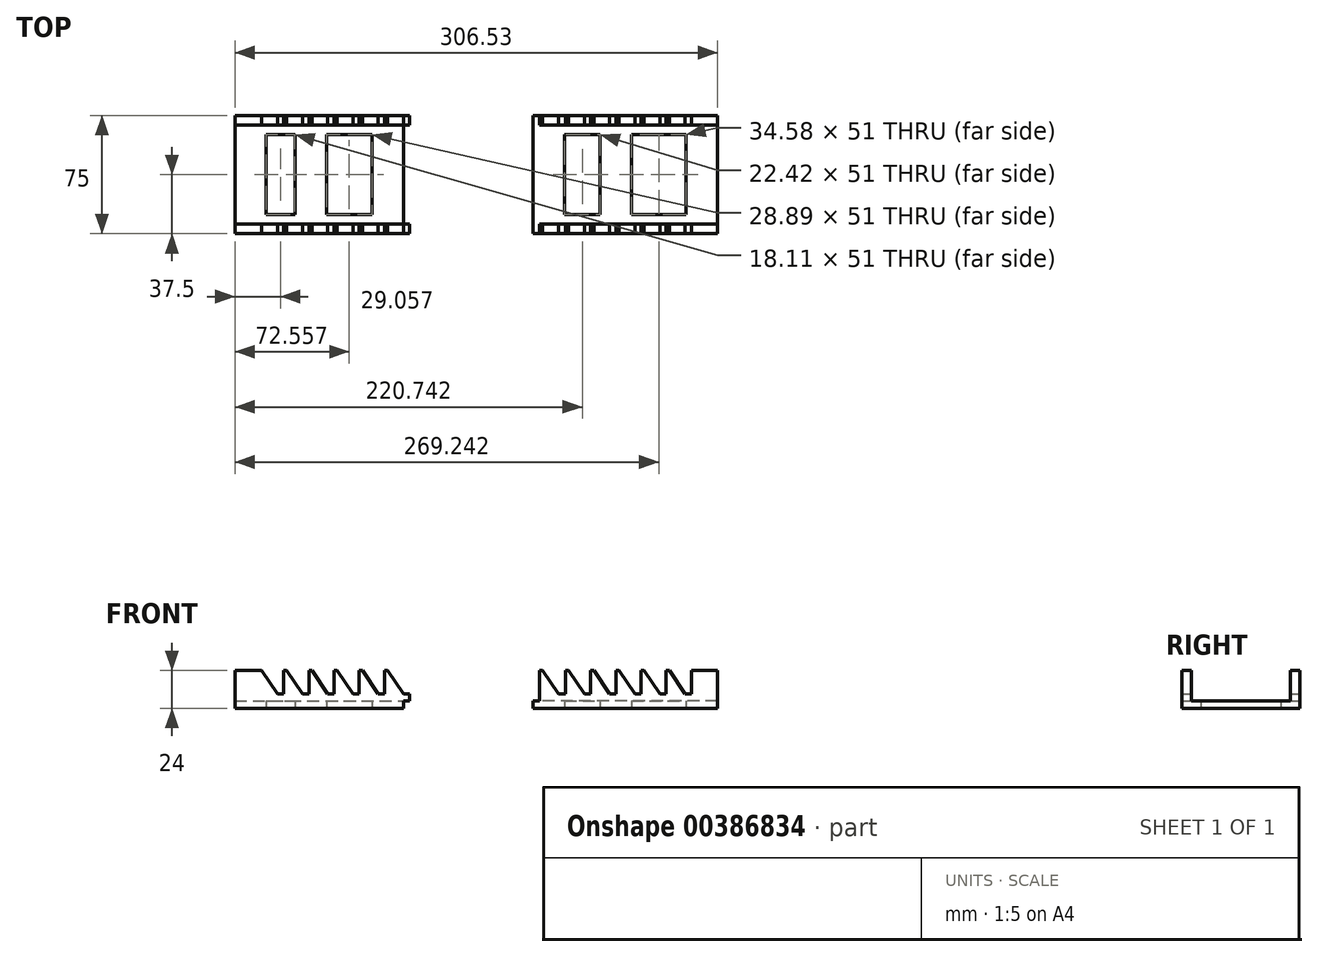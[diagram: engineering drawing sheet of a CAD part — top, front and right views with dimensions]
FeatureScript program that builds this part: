
annotation { "Feature Type Name" : "Feature", "Feature Type Description" : "" }
export const myFeature = defineFeature(function(context is Context, id is Id, definition is map)
    precondition{}
    {
        {
            var Q0;
            Q0=qCreatedBy(makeId("Front.planeOp"),FACE);
            var sketch = newSketch(context, id + "F0", { "sketchPlane" : qUnion([Q0])});
            skLineSegment(sketch, "E0", {"start": v(96, 24) * mm, "end": v(98, 24) * mm});
            skLineSegment(sketch, "E1", {"start": v(98, 24) * mm, "end": v(108, 9) * mm});
            skLineSegment(sketch, "E2", {"start": v(108, 9) * mm, "end": v(112.5, 9) * mm});
            skLineSegment(sketch, "E3", {"start": v(112.5, 9) * mm, "end": v(112.5, 24) * mm});
            skLineSegment(sketch, "E4", {"start": v(112.5, 24) * mm, "end": v(114.5, 24) * mm});
            skLineSegment(sketch, "E5", {"start": v(114.5, 24) * mm, "end": v(124.5, 9) * mm});
            skLineSegment(sketch, "E6", {"start": v(124.5, 9) * mm, "end": v(128.5, 9) * mm});
            skLineSegment(sketch, "E7", {"start": v(128.5, 9) * mm, "end": v(128.5, 24) * mm});
            skLineSegment(sketch, "E8", {"start": v(128.5, 24) * mm, "end": v(130.5, 24) * mm});
            skLineSegment(sketch, "E9", {"start": v(130.5, 24) * mm, "end": v(140.5, 9) * mm});
            skLineSegment(sketch, "E10", {"start": v(140.5, 9) * mm, "end": v(144.5, 9) * mm});
            skLineSegment(sketch, "E11", {"start": v(144.5, 9) * mm, "end": v(144.5, 24) * mm});
            skLineSegment(sketch, "E12", {"start": v(144.5, 24) * mm, "end": v(146.5, 24) * mm});
            skLineSegment(sketch, "E13", {"start": v(146.5, 24) * mm, "end": v(156.5, 9) * mm});
            skLineSegment(sketch, "E14", {"start": v(156.5, 9) * mm, "end": v(160.44, 9) * mm});
            skLineSegment(sketch, "E15", {"start": v(160.44, 9) * mm, "end": v(160.44, 24) * mm});
            skLineSegment(sketch, "E16", {"start": v(160.44, 24) * mm, "end": v(162.44, 24) * mm});
            skLineSegment(sketch, "E17", {"start": v(162.44, 24) * mm, "end": v(172.44, 9) * mm});
            skLineSegment(sketch, "E18", {"start": v(172.44, 9) * mm, "end": v(176.44, 9) * mm});
            skLineSegment(sketch, "E19", {"start": v(176.44, 9) * mm, "end": v(176.44, 24) * mm});
            skLineSegment(sketch, "E20", {"start": v(176.44, 24) * mm, "end": v(178.44, 24) * mm});
            skLineSegment(sketch, "E21", {"start": v(178.44, 24) * mm, "end": v(188.44, 9) * mm});
            skLineSegment(sketch, "E22", {"start": v(188.44, 9) * mm, "end": v(192.44, 9) * mm});
            skLineSegment(sketch, "E23", {"start": v(192.44, 9) * mm, "end": v(192.44, 24) * mm});
            skLineSegment(sketch, "E24", {"start": v(192.44, 24) * mm, "end": v(209, 24) * mm});
            skLineSegment(sketch, "E25.top", {"start": v(209, 0) * mm, "end": v(209.44, 0) * mm});
            skLineSegment(sketch, "E26.trimOffspring", {"start": v(108, 9) * mm, "end": v(112.5, 9) * mm, "construction": true});
            skLineSegment(sketch, "E27.trimOffspring", {"start": v(124.5, 9) * mm, "end": v(128.5, 9) * mm, "construction": true});
            skLineSegment(sketch, "E28.trimOffspring", {"start": v(140.5, 9) * mm, "end": v(144.5, 9) * mm, "construction": true});
            skLineSegment(sketch, "E29.trimOffspring", {"start": v(156.5, 9) * mm, "end": v(160.44, 9) * mm, "construction": true});
            skLineSegment(sketch, "E30.trimOffspring", {"start": v(188.44, 9) * mm, "end": v(192.44, 9) * mm, "construction": true});
            skLineSegment(sketch, "E31", {"start": v(96.1, 4.59) * mm, "end": v(92, 4.59) * mm});
            skLineSegment(sketch, "E32", {"start": v(92, 4.59) * mm, "end": v(92, 0) * mm});
            skLineSegment(sketch, "E33", {"start": v(-66.53, 24) * mm, "end": v(-64.53, 24) * mm});
            skLineSegment(sketch, "E34", {"start": v(-64.53, 24) * mm, "end": v(-54.53, 9) * mm});
            skLineSegment(sketch, "E35", {"start": v(-50.53, 9) * mm, "end": v(-50.53, 24) * mm});
            skLineSegment(sketch, "E36", {"start": v(-50.53, 24) * mm, "end": v(-48.53, 24) * mm});
            skLineSegment(sketch, "E37", {"start": v(-48.53, 24) * mm, "end": v(-38.53, 9) * mm});
            skLineSegment(sketch, "E38", {"start": v(-34.53, 9) * mm, "end": v(-34.53, 24) * mm});
            skLineSegment(sketch, "E39", {"start": v(-34.53, 24) * mm, "end": v(-32.53, 24) * mm});
            skLineSegment(sketch, "E40", {"start": v(-32.53, 24) * mm, "end": v(-22.52, 9) * mm});
            skLineSegment(sketch, "E41", {"start": v(-18.52, 9) * mm, "end": v(-18.52, 24) * mm});
            skLineSegment(sketch, "E42", {"start": v(-18.52, 24) * mm, "end": v(-16.52, 24) * mm});
            skLineSegment(sketch, "E43", {"start": v(-16.52, 24) * mm, "end": v(-6.52, 9) * mm});
            skLineSegment(sketch, "E44", {"start": v(-2.52, 9) * mm, "end": v(-2.52, 24) * mm});
            skLineSegment(sketch, "E45", {"start": v(-2.52, 24) * mm, "end": v(-0.52, 24) * mm});
            skLineSegment(sketch, "E46", {"start": v(-0.52, 24) * mm, "end": v(9.48, 9) * mm});
            skLineSegment(sketch, "E47", {"start": v(-66.53, 9) * mm, "end": v(-66.53, 24) * mm});
            skLineSegment(sketch, "E48", {"start": v(-97.53, 0) * mm, "end": v(-97.53, 24) * mm});
            skLineSegment(sketch, "E49", {"start": v(-70.53, 9) * mm, "end": v(-80.53, 24) * mm});
            skLineSegment(sketch, "E50", {"start": v(-97.53, 24) * mm, "end": v(-80.53, 24) * mm});
            skLineSegment(sketch, "E51", {"start": v(13.48, 9) * mm, "end": v(13.48, 4.5) * mm});
            skLineSegment(sketch, "E52", {"start": v(13.56, 4.59) * mm, "end": v(9.47, 4.59) * mm});
            skLineSegment(sketch, "E53", {"start": v(9.47, 4.59) * mm, "end": v(9.47, 0) * mm});
            skLineSegment(sketch, "E54", {"start": v(-97.53, 0) * mm, "end": v(9.47, 0) * mm});
            skLineSegment(sketch, "E55", {"start": v(-70.53, 9) * mm, "end": v(-66.53, 9) * mm});
            skLineSegment(sketch, "E56", {"start": v(-54.53, 9) * mm, "end": v(-50.53, 9) * mm});
            skLineSegment(sketch, "E57", {"start": v(-38.53, 9) * mm, "end": v(-34.53, 9) * mm});
            skLineSegment(sketch, "E58", {"start": v(-18.52, 9) * mm, "end": v(-22.52, 9) * mm});
            skLineSegment(sketch, "E59", {"start": v(-6.52, 9) * mm, "end": v(-2.52, 9) * mm});
            skLineSegment(sketch, "E60", {"start": v(9.48, 9) * mm, "end": v(13.48, 9) * mm});
            skLineSegment(sketch, "E61", {"start": v(92, 0) * mm, "end": v(209, 0) * mm});
            skLineSegment(sketch, "E62", {"start": v(96, 24) * mm, "end": v(96.1, 4.59) * mm});
            skLineSegment(sketch, "E63", {"start": v(209, 24) * mm, "end": v(209, 0) * mm});
            skSolve(sketch);
        }
        {
            var Q0;
            Q0=makeQuery(id+"F0.imprint","IMPRINT",FACE,{"disambiguationData":[TD([[makeQuery(id+"F0.imprint","IMPRINT",EDGE,{"derivedFrom":sQuery(id+"F0.wireOp",EDGE,"E33")}),-1.0]])]});
            var Q1;
            Q1=makeQuery(id+"F0.imprint","IMPRINT",FACE,{"disambiguationData":[TD([[makeQuery(id+"F0.imprint","IMPRINT",EDGE,{"derivedFrom":sQuery(id+"F0.wireOp",EDGE,"E0")}),-1.0]])]});
            extrude(context, id + "F1", {"entities" : qUnion([Q0, Q1]), "depth" : 75 * mm});
        }
        {
            var Q0;
            Q0=makeQuery(id+"F1.opExtrude","SWEPT_FACE",FACE,{"disambiguationData":[OSD([sQuery(id+"F0.wireOp",EDGE,"E54")])]});
            var sketch = newSketch(context, id + "F2", { "sketchPlane" : qUnion([Q0])});
            skLineSegment(sketch, "E64.bottom", {"start": v(-97.53, 6) * mm, "end": v(209, 6) * mm});
            skLineSegment(sketch, "E64.top", {"start": v(-97.53, 69) * mm, "end": v(209, 69) * mm});
            skLineSegment(sketch, "E64.left", {"start": v(-97.53, 6) * mm, "end": v(-97.53, 69) * mm});
            skLineSegment(sketch, "E64.right", {"start": v(209, 6) * mm, "end": v(209, 69) * mm});
            skSolve(sketch);
        }
        {
            var Q0;
            {var subQ0=sQuery(id+"F2.wireOp",EDGE,"E64.right");Q0=makeQuery(id+"F2.imprint","IMPRINT",FACE,{"disambiguationData":[TD([[makeQuery(id+"F2.imprint","IMPRINT",EDGE,{"derivedFrom":subQ0}),1.0]])]});}
            var Q1;
            {var subQ0=sQuery(id+"F2.wireOp",EDGE,"E64.left");Q1=makeQuery(id+"F2.imprint","IMPRINT",FACE,{"disambiguationData":[TD([[makeQuery(id+"F2.imprint","IMPRINT",EDGE,{"derivedFrom":subQ0}),1.0]])]});}
            extrude(context, id + "F3", {"entities" : qUnion([Q0, Q1]), "operationType" : NewBodyOperationType.REMOVE, "endBound" : BoundingType.THROUGH_ALL, "oppositeDirection" : true, "depth" : 25 * mm});
        }
        {
            var Q0;
            Q0=makeQuery(id+"F1.opExtrude","SWEPT_FACE",FACE,{"disambiguationData":[OSD([sQuery(id+"F0.wireOp",EDGE,"E54")])]});
            var sketch = newSketch(context, id + "F4", { "sketchPlane" : qUnion([Q0])});
            skLineSegment(sketch, "E65.bottom", {"start": v(13.48, 69) * mm, "end": v(-97.53, 69) * mm});
            skLineSegment(sketch, "E65.top", {"start": v(13.48, 6) * mm, "end": v(-97.53, 6) * mm});
            skLineSegment(sketch, "E65.left", {"start": v(13.48, 69) * mm, "end": v(13.48, 6) * mm});
            skLineSegment(sketch, "E65.right", {"start": v(-97.53, 69) * mm, "end": v(-97.53, 6) * mm});
            skSolve(sketch);
        }
        {
            var Q0;
            {var subQ0=sQuery(id+"F4.wireOp",EDGE,"E65.right");Q0=makeQuery(id+"F4.imprint","IMPRINT",FACE,{"disambiguationData":[TD([[makeQuery(id+"F4.imprint","IMPRINT",EDGE,{"derivedFrom":subQ0}),1.0]])]});}
            var Q1;
            {var subQ0=sQuery(id+"F4.wireOp",EDGE,"E65.left");Q1=makeQuery(id+"F4.imprint","IMPRINT",FACE,{"disambiguationData":[TD([[makeQuery(id+"F4.imprint","IMPRINT",EDGE,{"derivedFrom":subQ0}),-1.0]])]});}
            extrude(context, id + "F5", {"entities" : qUnion([Q0, Q1]), "operationType" : NewBodyOperationType.REMOVE, "endBound" : BoundingType.THROUGH_ALL, "oppositeDirection" : true, "depth" : 25 * mm});
        }
        {
            var Q0;
            {var subQ1=sQuery(id+"F0.wireOp",EDGE,"E53");Q0=makeQuery(id+"F5.boolean.opBoolean","SPLIT",FACE,{"disambiguationData":[TD([makeQuery(id+"F5.opExtrude","SWEPT_FACE",FACE,{"disambiguationData":[OSD([sQuery(id+"F4.wireOp",EDGE,"E65.bottom")])]})])],"derivedFrom":makeQuery(id+"F1.opExtrude","SWEPT_FACE",FACE,{"disambiguationData":[OSD([subQ1])]})});}
            var sketch = newSketch(context, id + "F6", { "sketchPlane" : qUnion([Q0])});
            skLineSegment(sketch, "E66.bottom", {"start": v(-69, 4.59) * mm, "end": v(-6, 4.59) * mm});
            skLineSegment(sketch, "E66.top", {"start": v(-69, 0) * mm, "end": v(-6, 0) * mm});
            skLineSegment(sketch, "E66.left", {"start": v(-69, 4.59) * mm, "end": v(-69, 0) * mm});
            skLineSegment(sketch, "E66.right", {"start": v(-6, 4.59) * mm, "end": v(-6, 0) * mm});
            skSolve(sketch);
        }
        {
            var Q0;
            Q0=makeQuery(id+"F6.imprint","IMPRINT",FACE,{"disambiguationData":[TD([[makeQuery(id+"F6.imprint","IMPRINT",EDGE,{"derivedFrom":sQuery(id+"F6.wireOp",EDGE,"E66.bottom")}),-1.0]])]});
            extrude(context, id + "F7", {"entities" : qUnion([Q0]), "oppositeDirection" : true, "depth" : 107 * mm});
        }
        {
            var Q0;
            {var subQ1=sQuery(id+"F0.wireOp",EDGE,"E32");Q0=makeQuery(id+"F3.boolean.opBoolean","SPLIT",FACE,{"disambiguationData":[TD([makeQuery(id+"F3.opExtrude","SWEPT_FACE",FACE,{"disambiguationData":[OSD([sQuery(id+"F2.wireOp",EDGE,"E64.top")])]})])],"derivedFrom":makeQuery(id+"F1.opExtrude","SWEPT_FACE",FACE,{"disambiguationData":[OSD([subQ1])]})});}
            var sketch = newSketch(context, id + "F8", { "sketchPlane" : qUnion([Q0])});
            skLineSegment(sketch, "E67.bottom", {"start": v(69, 4.59) * mm, "end": v(6, 4.59) * mm});
            skLineSegment(sketch, "E67.top", {"start": v(69, 0) * mm, "end": v(6, 0) * mm});
            skLineSegment(sketch, "E67.left", {"start": v(69, 4.59) * mm, "end": v(69, 0) * mm});
            skLineSegment(sketch, "E67.right", {"start": v(6, 4.59) * mm, "end": v(6, 0) * mm});
            skSolve(sketch);
        }
        {
            var Q0;
            Q0=makeQuery(id+"F8.imprint","IMPRINT",FACE,{"disambiguationData":[TD([[makeQuery(id+"F8.imprint","IMPRINT",EDGE,{"derivedFrom":sQuery(id+"F8.wireOp",EDGE,"E67.bottom")}),1.0]])]});
            extrude(context, id + "F9", {"entities" : qUnion([Q0]), "oppositeDirection" : true, "depth" : 117 * mm});
        }
        {
            var Q0;
            Q0=makeQuery(id+"F3.boolean.opBoolean","SPLIT",BODY,{"disambiguationData":[OD(0.0)],"derivedFrom":makeQuery(id+"F1.opExtrude","SWEPT_BODY",BODY,{"disambiguationData":[OSD([sQuery(id+"F0.wireOp",EDGE,"E0"),sQuery(id+"F0.wireOp",EDGE,"E1"),sQuery(id+"F0.wireOp",EDGE,"E3"),sQuery(id+"F0.wireOp",EDGE,"E4"),sQuery(id+"F0.wireOp",EDGE,"E5"),sQuery(id+"F0.wireOp",EDGE,"E7"),sQuery(id+"F0.wireOp",EDGE,"E8"),sQuery(id+"F0.wireOp",EDGE,"E9"),sQuery(id+"F0.wireOp",EDGE,"E11"),sQuery(id+"F0.wireOp",EDGE,"E12"),sQuery(id+"F0.wireOp",EDGE,"E13"),sQuery(id+"F0.wireOp",EDGE,"E15"),sQuery(id+"F0.wireOp",EDGE,"E16"),sQuery(id+"F0.wireOp",EDGE,"E17"),sQuery(id+"F0.wireOp",EDGE,"E19"),sQuery(id+"F0.wireOp",EDGE,"E20"),sQuery(id+"F0.wireOp",EDGE,"E21"),sQuery(id+"F0.wireOp",EDGE,"E23"),sQuery(id+"F0.wireOp",EDGE,"E24"),sQuery(id+"F0.wireOp",EDGE,"E2"),sQuery(id+"F0.wireOp",EDGE,"E6"),sQuery(id+"F0.wireOp",EDGE,"E10"),sQuery(id+"F0.wireOp",EDGE,"E14"),sQuery(id+"F0.wireOp",EDGE,"E18"),sQuery(id+"F0.wireOp",EDGE,"E22"),sQuery(id+"F0.wireOp",EDGE,"E31"),sQuery(id+"F0.wireOp",EDGE,"E32"),sQuery(id+"F0.wireOp",EDGE,"E61"),sQuery(id+"F0.wireOp",EDGE,"E62"),sQuery(id+"F0.wireOp",EDGE,"E63")])]})});
            var Q1;
            Q1=makeQuery(id+"F3.boolean.opBoolean","SPLIT",BODY,{"disambiguationData":[OD(1.0)],"derivedFrom":makeQuery(id+"F1.opExtrude","SWEPT_BODY",BODY,{"disambiguationData":[OSD([sQuery(id+"F0.wireOp",EDGE,"E0"),sQuery(id+"F0.wireOp",EDGE,"E1"),sQuery(id+"F0.wireOp",EDGE,"E3"),sQuery(id+"F0.wireOp",EDGE,"E4"),sQuery(id+"F0.wireOp",EDGE,"E5"),sQuery(id+"F0.wireOp",EDGE,"E7"),sQuery(id+"F0.wireOp",EDGE,"E8"),sQuery(id+"F0.wireOp",EDGE,"E9"),sQuery(id+"F0.wireOp",EDGE,"E11"),sQuery(id+"F0.wireOp",EDGE,"E12"),sQuery(id+"F0.wireOp",EDGE,"E13"),sQuery(id+"F0.wireOp",EDGE,"E15"),sQuery(id+"F0.wireOp",EDGE,"E16"),sQuery(id+"F0.wireOp",EDGE,"E17"),sQuery(id+"F0.wireOp",EDGE,"E19"),sQuery(id+"F0.wireOp",EDGE,"E20"),sQuery(id+"F0.wireOp",EDGE,"E21"),sQuery(id+"F0.wireOp",EDGE,"E23"),sQuery(id+"F0.wireOp",EDGE,"E24"),sQuery(id+"F0.wireOp",EDGE,"E2"),sQuery(id+"F0.wireOp",EDGE,"E6"),sQuery(id+"F0.wireOp",EDGE,"E10"),sQuery(id+"F0.wireOp",EDGE,"E14"),sQuery(id+"F0.wireOp",EDGE,"E18"),sQuery(id+"F0.wireOp",EDGE,"E22"),sQuery(id+"F0.wireOp",EDGE,"E31"),sQuery(id+"F0.wireOp",EDGE,"E32"),sQuery(id+"F0.wireOp",EDGE,"E61"),sQuery(id+"F0.wireOp",EDGE,"E62"),sQuery(id+"F0.wireOp",EDGE,"E63")])]})});
            var Q2;
            Q2=makeQuery(id+"F9.opExtrude","SWEPT_BODY",BODY,{"disambiguationData":[OSD([sQuery(id+"F8.wireOp",EDGE,"E67.bottom"),sQuery(id+"F8.wireOp",EDGE,"E67.top"),sQuery(id+"F8.wireOp",EDGE,"E67.left"),sQuery(id+"F8.wireOp",EDGE,"E67.right")])]});
            booleanBodies(context, id + "F10", {"operationType" : BooleanOperationType.UNION, "tools" : qUnion([Q0, Q1, Q2])});
        }
        {
            var Q0;
            Q0=makeQuery(id+"F5.boolean.opBoolean","SPLIT",BODY,{"disambiguationData":[OD(0.0)],"derivedFrom":makeQuery(id+"F1.opExtrude","SWEPT_BODY",BODY,{"disambiguationData":[OSD([sQuery(id+"F0.wireOp",EDGE,"E33"),sQuery(id+"F0.wireOp",EDGE,"E34"),sQuery(id+"F0.wireOp",EDGE,"E35"),sQuery(id+"F0.wireOp",EDGE,"E36"),sQuery(id+"F0.wireOp",EDGE,"E37"),sQuery(id+"F0.wireOp",EDGE,"E38"),sQuery(id+"F0.wireOp",EDGE,"E39"),sQuery(id+"F0.wireOp",EDGE,"E40"),sQuery(id+"F0.wireOp",EDGE,"E41"),sQuery(id+"F0.wireOp",EDGE,"E42"),sQuery(id+"F0.wireOp",EDGE,"E43"),sQuery(id+"F0.wireOp",EDGE,"E44"),sQuery(id+"F0.wireOp",EDGE,"E45"),sQuery(id+"F0.wireOp",EDGE,"E46"),sQuery(id+"F0.wireOp",EDGE,"E47"),sQuery(id+"F0.wireOp",EDGE,"E48"),sQuery(id+"F0.wireOp",EDGE,"E49"),sQuery(id+"F0.wireOp",EDGE,"E50"),sQuery(id+"F0.wireOp",EDGE,"E51"),sQuery(id+"F0.wireOp",EDGE,"E52"),sQuery(id+"F0.wireOp",EDGE,"E53"),sQuery(id+"F0.wireOp",EDGE,"E54"),sQuery(id+"F0.wireOp",EDGE,"E55"),sQuery(id+"F0.wireOp",EDGE,"E56"),sQuery(id+"F0.wireOp",EDGE,"E57"),sQuery(id+"F0.wireOp",EDGE,"E58"),sQuery(id+"F0.wireOp",EDGE,"E59"),sQuery(id+"F0.wireOp",EDGE,"E60")])]})});
            var Q1;
            Q1=makeQuery(id+"F5.boolean.opBoolean","SPLIT",BODY,{"disambiguationData":[OD(1.0)],"derivedFrom":makeQuery(id+"F1.opExtrude","SWEPT_BODY",BODY,{"disambiguationData":[OSD([sQuery(id+"F0.wireOp",EDGE,"E33"),sQuery(id+"F0.wireOp",EDGE,"E34"),sQuery(id+"F0.wireOp",EDGE,"E35"),sQuery(id+"F0.wireOp",EDGE,"E36"),sQuery(id+"F0.wireOp",EDGE,"E37"),sQuery(id+"F0.wireOp",EDGE,"E38"),sQuery(id+"F0.wireOp",EDGE,"E39"),sQuery(id+"F0.wireOp",EDGE,"E40"),sQuery(id+"F0.wireOp",EDGE,"E41"),sQuery(id+"F0.wireOp",EDGE,"E42"),sQuery(id+"F0.wireOp",EDGE,"E43"),sQuery(id+"F0.wireOp",EDGE,"E44"),sQuery(id+"F0.wireOp",EDGE,"E45"),sQuery(id+"F0.wireOp",EDGE,"E46"),sQuery(id+"F0.wireOp",EDGE,"E47"),sQuery(id+"F0.wireOp",EDGE,"E48"),sQuery(id+"F0.wireOp",EDGE,"E49"),sQuery(id+"F0.wireOp",EDGE,"E50"),sQuery(id+"F0.wireOp",EDGE,"E51"),sQuery(id+"F0.wireOp",EDGE,"E52"),sQuery(id+"F0.wireOp",EDGE,"E53"),sQuery(id+"F0.wireOp",EDGE,"E54"),sQuery(id+"F0.wireOp",EDGE,"E55"),sQuery(id+"F0.wireOp",EDGE,"E56"),sQuery(id+"F0.wireOp",EDGE,"E57"),sQuery(id+"F0.wireOp",EDGE,"E58"),sQuery(id+"F0.wireOp",EDGE,"E59"),sQuery(id+"F0.wireOp",EDGE,"E60")])]})});
            var Q2;
            Q2=makeQuery(id+"F7.opExtrude","SWEPT_BODY",BODY,{"disambiguationData":[OSD([sQuery(id+"F6.wireOp",EDGE,"E66.bottom"),sQuery(id+"F6.wireOp",EDGE,"E66.top"),sQuery(id+"F6.wireOp",EDGE,"E66.left"),sQuery(id+"F6.wireOp",EDGE,"E66.right")])]});
            booleanBodies(context, id + "F11", {"operationType" : BooleanOperationType.UNION, "tools" : qUnion([Q0, Q1, Q2])});
        }
        {
            var Q0;
            {var subQ2=sQuery(id+"F0.wireOp",EDGE,"E61");var subQ32=makeQuery(id+"F1.opExtrude","SWEPT_FACE",FACE,{"disambiguationData":[OSD([subQ2])]});Q0=makeQuery(id+"F10.opBoolean","MERGE",FACE,{"derivedFrom":[makeQuery(id+"F3.boolean.opBoolean","SPLIT",FACE,{"disambiguationData":[TD([makeQuery(id+"F3.opExtrude","SWEPT_FACE",FACE,{"disambiguationData":[OSD([sQuery(id+"F2.wireOp",EDGE,"E64.bottom")])]})])],"derivedFrom":subQ32}),makeQuery(id+"F3.boolean.opBoolean","SPLIT",FACE,{"disambiguationData":[TD([makeQuery(id+"F3.opExtrude","SWEPT_FACE",FACE,{"disambiguationData":[OSD([sQuery(id+"F2.wireOp",EDGE,"E64.top")])]})])],"derivedFrom":subQ32}),makeQuery(id+"F9.opExtrude","SWEPT_FACE",FACE,{"disambiguationData":[OSD([sQuery(id+"F8.wireOp",EDGE,"E67.top")])]})]});}
            var sketch = newSketch(context, id + "F12", { "sketchPlane" : qUnion([Q0])});
            skLineSegment(sketch, "E68.bottom", {"start": v(92, 63) * mm, "end": v(209, 63) * mm, "construction": true});
            skLineSegment(sketch, "E68.top", {"start": v(92, 12) * mm, "end": v(209, 12) * mm, "construction": true});
            skLineSegment(sketch, "E68.left", {"start": v(92, 63) * mm, "end": v(92, 12) * mm, "construction": true});
            skLineSegment(sketch, "E68.right", {"start": v(209, 63) * mm, "end": v(209, 12) * mm, "construction": true});
            skLineSegment(sketch, "E69.bottom", {"start": v(112, 63) * mm, "end": v(134.42, 63) * mm});
            skLineSegment(sketch, "E69.top", {"start": v(112, 12) * mm, "end": v(134.42, 12) * mm});
            skLineSegment(sketch, "E69.left", {"start": v(112, 63) * mm, "end": v(112, 12) * mm});
            skLineSegment(sketch, "E69.right", {"start": v(134.42, 63) * mm, "end": v(134.42, 12) * mm});
            skLineSegment(sketch, "E70.bottom", {"start": v(154.42, 63) * mm, "end": v(189, 63) * mm});
            skLineSegment(sketch, "E70.top", {"start": v(154.42, 12) * mm, "end": v(189, 12) * mm});
            skLineSegment(sketch, "E70.left", {"start": v(154.42, 63) * mm, "end": v(154.42, 12) * mm});
            skLineSegment(sketch, "E70.right", {"start": v(189, 63) * mm, "end": v(189, 12) * mm});
            skSolve(sketch);
        }
        {
            var Q0;
            Q0=makeQuery(id+"F12.imprint","IMPRINT",FACE,{"disambiguationData":[TD([[makeQuery(id+"F12.imprint","IMPRINT",EDGE,{"derivedFrom":sQuery(id+"F12.wireOp",EDGE,"E69.bottom")}),-1.0]])]});
            var Q1;
            Q1=makeQuery(id+"F12.imprint","IMPRINT",FACE,{"disambiguationData":[TD([[makeQuery(id+"F12.imprint","IMPRINT",EDGE,{"derivedFrom":sQuery(id+"F12.wireOp",EDGE,"E70.bottom")}),-1.0]])]});
            extrude(context, id + "F13", {"entities" : qUnion([Q0, Q1]), "operationType" : NewBodyOperationType.REMOVE, "endBound" : BoundingType.THROUGH_ALL, "oppositeDirection" : true, "depth" : 25 * mm});
        }
        {
            var Q0;
            {var subQ6=sQuery(id+"F0.wireOp",EDGE,"E54");var subQ30=makeQuery(id+"F1.opExtrude","SWEPT_FACE",FACE,{"disambiguationData":[OSD([subQ6])]});Q0=makeQuery(id+"F11.opBoolean","MERGE",FACE,{"derivedFrom":[makeQuery(id+"F5.boolean.opBoolean","SPLIT",FACE,{"disambiguationData":[TD([makeQuery(id+"F5.opExtrude","SWEPT_FACE",FACE,{"disambiguationData":[OSD([sQuery(id+"F4.wireOp",EDGE,"E65.top")])]})])],"derivedFrom":subQ30}),makeQuery(id+"F5.boolean.opBoolean","SPLIT",FACE,{"disambiguationData":[TD([makeQuery(id+"F5.opExtrude","SWEPT_FACE",FACE,{"disambiguationData":[OSD([sQuery(id+"F4.wireOp",EDGE,"E65.bottom")])]})])],"derivedFrom":subQ30}),makeQuery(id+"F7.opExtrude","SWEPT_FACE",FACE,{"disambiguationData":[OSD([sQuery(id+"F6.wireOp",EDGE,"E66.top")])]})]});}
            var sketch = newSketch(context, id + "F14", { "sketchPlane" : qUnion([Q0])});
            skLineSegment(sketch, "E71.bottom", {"start": v(-97.53, 63) * mm, "end": v(9.47, 63) * mm, "construction": true});
            skLineSegment(sketch, "E71.top", {"start": v(-97.53, 12) * mm, "end": v(9.47, 12) * mm, "construction": true});
            skLineSegment(sketch, "E71.left", {"start": v(-97.53, 63) * mm, "end": v(-97.53, 12) * mm, "construction": true});
            skLineSegment(sketch, "E71.right", {"start": v(9.47, 63) * mm, "end": v(9.47, 12) * mm, "construction": true});
            skLineSegment(sketch, "E72.bottom", {"start": v(-77.53, 63) * mm, "end": v(-59.42, 63) * mm});
            skLineSegment(sketch, "E72.top", {"start": v(-77.53, 12) * mm, "end": v(-59.42, 12) * mm});
            skLineSegment(sketch, "E72.left", {"start": v(-77.53, 63) * mm, "end": v(-77.53, 12) * mm});
            skLineSegment(sketch, "E72.right", {"start": v(-59.42, 63) * mm, "end": v(-59.42, 12) * mm});
            skLineSegment(sketch, "E73.bottom", {"start": v(-39.42, 63) * mm, "end": v(-10.53, 63) * mm});
            skLineSegment(sketch, "E73.top", {"start": v(-39.42, 12) * mm, "end": v(-10.53, 12) * mm});
            skLineSegment(sketch, "E73.left", {"start": v(-39.42, 63) * mm, "end": v(-39.42, 12) * mm});
            skLineSegment(sketch, "E73.right", {"start": v(-10.53, 63) * mm, "end": v(-10.53, 12) * mm});
            skSolve(sketch);
        }
        {
            var Q0;
            Q0=makeQuery(id+"F14.imprint","IMPRINT",FACE,{"disambiguationData":[TD([[makeQuery(id+"F14.imprint","IMPRINT",EDGE,{"derivedFrom":sQuery(id+"F14.wireOp",EDGE,"E72.bottom")}),-1.0]])]});
            var Q1;
            Q1=makeQuery(id+"F14.imprint","IMPRINT",FACE,{"disambiguationData":[TD([[makeQuery(id+"F14.imprint","IMPRINT",EDGE,{"derivedFrom":sQuery(id+"F14.wireOp",EDGE,"E73.bottom")}),-1.0]])]});
            extrude(context, id + "F15", {"entities" : qUnion([Q0, Q1]), "operationType" : NewBodyOperationType.REMOVE, "endBound" : BoundingType.THROUGH_ALL, "oppositeDirection" : true, "depth" : 25 * mm});
        }
    });
